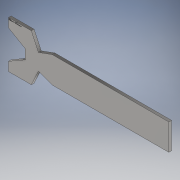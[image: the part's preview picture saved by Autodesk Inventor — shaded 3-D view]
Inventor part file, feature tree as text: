
AUTODESK INVENTOR PART (.ipt)
format: ipt  version: 2021 (Build 250183000, 183)  size: 1,019,904 bytes
history: native  units: mm
features: sketch x2, extrude x1, emboss x1
ambient origin geometry x8: Origin, YZ Plane, XZ Plane, XY Plane, X Axis, Y Axis, Z Axis, Center Point
bodies: Solid1 (feature_tree)
feature tree (4):
  extrude  "Extrusion1"  Depth=18.0mm
  emboss  "Emboss1"
  sketch  "Sketch1"  dims[d0=80.0mm d1=18.0mm]
  sketch  "Sketch2"  dims[d2=30.0mm d3=0.0mm d4=7.0mm d5=7.0mm d6=27.925268mm d7=27.925268mm d8=10.0mm d9=10.0mm d10=20.071286mm d11=20.071286mm d12=6.0mm d13=120.0deg d14=6.0mm d15=120.0deg d16=30.0mm d17=1.905mm d18=0.0mm d19=1.0mm d20=0.0mm]
